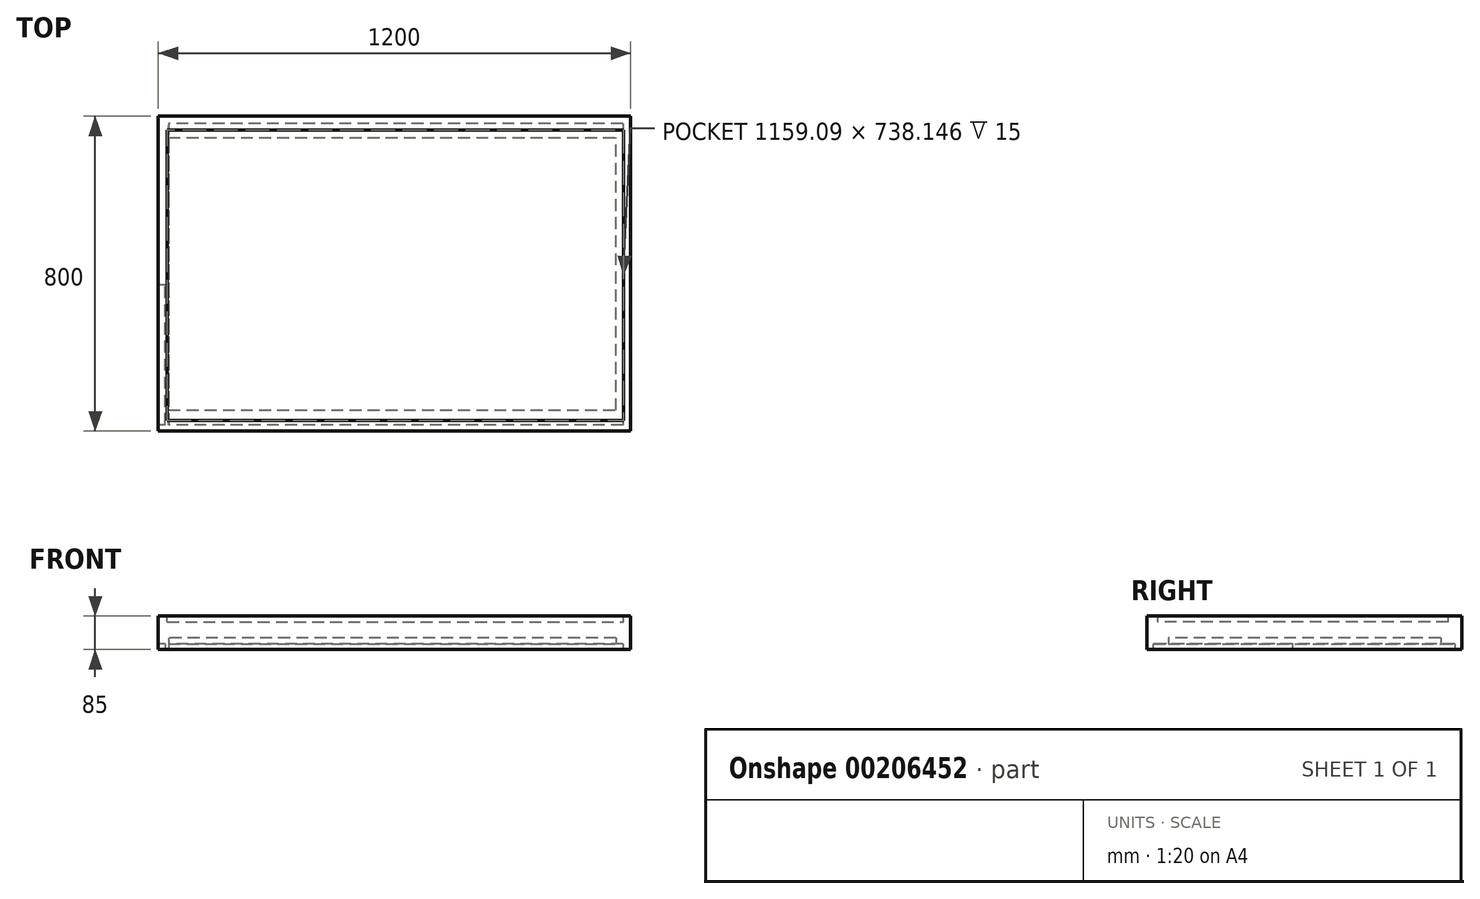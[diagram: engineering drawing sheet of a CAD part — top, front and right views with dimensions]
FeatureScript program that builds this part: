
annotation { "Feature Type Name" : "Feature", "Feature Type Description" : "" }
export const myFeature = defineFeature(function(context is Context, id is Id, definition is map)
    precondition{}
    {
        {
            var Q0;
            Q0=qCreatedBy(makeId("Top.planeOp"),FACE);
            var sketch = newSketch(context, id + "F0", { "sketchPlane" : qUnion([Q0])});
            skLineSegment(sketch, "E0.bottom", {"start": v(0, 0) * mm, "end": v(1200, 0) * mm});
            skLineSegment(sketch, "E0.top", {"start": v(0, 800) * mm, "end": v(1200, 800) * mm});
            skLineSegment(sketch, "E0.left", {"start": v(0, 0) * mm, "end": v(0, 800) * mm});
            skLineSegment(sketch, "E0.right", {"start": v(1200, 0) * mm, "end": v(1200, 800) * mm});
            skSolve(sketch);
        }
        {
            var Q0;
            Q0=makeQuery(id+"F0.imprint","IMPRINT",FACE,{"disambiguationData":[TD([[makeQuery(id+"F0.imprint","IMPRINT",EDGE,{"derivedFrom":sQuery(id+"F0.wireOp",EDGE,"E0.bottom")}),1.0]])]});
            extrude(context, id + "F1", {"entities" : qUnion([Q0]), "depth" : 60 * mm});
        }
        {
            var Q0;
            Q0=makeQuery(id+"F1.opExtrude","CAP_FACE",FACE,{"disambiguationData":[OSD([sQuery(id+"F0.wireOp",EDGE,"E0.bottom"),sQuery(id+"F0.wireOp",EDGE,"E0.top"),sQuery(id+"F0.wireOp",EDGE,"E0.left"),sQuery(id+"F0.wireOp",EDGE,"E0.right")])],"isStart":false});
            var sketch = newSketch(context, id + "F2", { "sketchPlane" : qUnion([Q0])});
            skLineSegment(sketch, "E1.bottom", {"start": v(37.83, 41.32) * mm, "end": v(1170.7, 41.32) * mm});
            skLineSegment(sketch, "E1.top", {"start": v(37.83, 752.02) * mm, "end": v(1170.7, 752.02) * mm});
            skLineSegment(sketch, "E1.left", {"start": v(37.83, 41.32) * mm, "end": v(37.83, 752.02) * mm});
            skLineSegment(sketch, "E1.right", {"start": v(1170.7, 41.32) * mm, "end": v(1170.7, 752.02) * mm});
            skSolve(sketch);
        }
        {
            var Q0;
            Q0=sQuery(id+"F2.wireOp",EDGE,"E1.top");
            var Q1;
            Q1=sQuery(id+"F2.wireOp",EDGE,"E1.left");
            var Q2;
            Q2=sQuery(id+"F2.wireOp",EDGE,"E1.bottom");
            var Q3;
            Q3=sQuery(id+"F2.wireOp",EDGE,"E1.right");
            extrude(context, id + "F3", {"bodyType" : ToolBodyType.SURFACE, "surfaceEntities" : qUnion([Q0, Q1, Q2, Q3]), "depth" : 30 * mm});
        }
        {
            var Q0;
            Q0=makeQuery(id+"F1.opExtrude","CAP_FACE",FACE,{"disambiguationData":[OSD([sQuery(id+"F0.wireOp",EDGE,"E0.bottom"),sQuery(id+"F0.wireOp",EDGE,"E0.top"),sQuery(id+"F0.wireOp",EDGE,"E0.left"),sQuery(id+"F0.wireOp",EDGE,"E0.right")])],"isStart":true});
            extrude(context, id + "F4", {"entities" : qUnion([Q0]), "operationType" : NewBodyOperationType.ADD, "depth" : 25 * mm});
        }
        {
            var Q0;
            Q0=makeQuery(id+"F4.opExtrude","CAP_FACE",FACE,{"disambiguationData":[OSD([sQuery(id+"F0.wireOp",EDGE,"E0.bottom"),sQuery(id+"F0.wireOp",EDGE,"E0.top"),sQuery(id+"F0.wireOp",EDGE,"E0.left"),sQuery(id+"F0.wireOp",EDGE,"E0.right")])],"isStart":false});
            var sketch = newSketch(context, id + "F5", { "sketchPlane" : qUnion([Q0])});
            skLineSegment(sketch, "E2.bottom", {"start": v(1162.82, -746.26) * mm, "end": v(25.87, -746.26) * mm});
            skLineSegment(sketch, "E2.top", {"start": v(1162.82, -53.64) * mm, "end": v(25.87, -53.64) * mm});
            skLineSegment(sketch, "E2.left", {"start": v(1162.82, -746.26) * mm, "end": v(1162.82, -53.64) * mm});
            skLineSegment(sketch, "E2.right", {"start": v(25.87, -746.26) * mm, "end": v(25.87, -53.64) * mm});
            skSolve(sketch);
        }
        {
            var Q0;
            Q0=makeQuery(id+"F5.imprint","IMPRINT",FACE,{"disambiguationData":[TD([[makeQuery(id+"F5.imprint","IMPRINT",EDGE,{"derivedFrom":sQuery(id+"F5.wireOp",EDGE,"E2.bottom")}),-1.0]])]});
            extrude(context, id + "F6", {"entities" : qUnion([Q0]), "operationType" : NewBodyOperationType.REMOVE, "oppositeDirection" : true, "depth" : 30 * mm});
        }
        {
            var Q0;
            Q0=makeQuery(id+"F1.opExtrude","CAP_FACE",FACE,{"disambiguationData":[OSD([sQuery(id+"F0.wireOp",EDGE,"E0.bottom"),sQuery(id+"F0.wireOp",EDGE,"E0.top"),sQuery(id+"F0.wireOp",EDGE,"E0.left"),sQuery(id+"F0.wireOp",EDGE,"E0.right")])],"isStart":false});
            var sketch = newSketch(context, id + "F7", { "sketchPlane" : qUnion([Q0])});
            skLineSegment(sketch, "E3.bottom", {"start": v(22.8, 765.04) * mm, "end": v(1181.9, 765.04) * mm});
            skLineSegment(sketch, "E3.top", {"start": v(22.8, 26.9) * mm, "end": v(1181.9, 26.9) * mm});
            skLineSegment(sketch, "E3.left", {"start": v(22.8, 765.04) * mm, "end": v(22.8, 26.9) * mm});
            skLineSegment(sketch, "E3.right", {"start": v(1181.9, 765.04) * mm, "end": v(1181.9, 26.9) * mm});
            skSolve(sketch);
        }
        {
            var Q0;
            Q0=makeQuery(id+"F7.imprint","IMPRINT",FACE,{"disambiguationData":[TD([[makeQuery(id+"F7.imprint","IMPRINT",EDGE,{"derivedFrom":sQuery(id+"F7.wireOp",EDGE,"E3.bottom")}),-1.0]])]});
            extrude(context, id + "F8", {"entities" : qUnion([Q0]), "operationType" : NewBodyOperationType.REMOVE, "oppositeDirection" : true, "depth" : 15 * mm});
        }
        {
            var Q0;
            Q0=makeQuery(id+"F4.opExtrude","CAP_FACE",FACE,{"disambiguationData":[OSD([sQuery(id+"F0.wireOp",EDGE,"E0.bottom"),sQuery(id+"F0.wireOp",EDGE,"E0.top"),sQuery(id+"F0.wireOp",EDGE,"E0.left"),sQuery(id+"F0.wireOp",EDGE,"E0.right")])],"isStart":false});
            var sketch = newSketch(context, id + "F9", { "sketchPlane" : qUnion([Q0])});
            skLineSegment(sketch, "E4.bottom", {"start": v(25.87, -31.78) * mm, "end": v(1008.33, -31.78) * mm});
            skLineSegment(sketch, "E4.top", {"start": v(25.87, -622.3) * mm, "end": v(1008.33, -622.3) * mm});
            skLineSegment(sketch, "E4.left", {"start": v(25.87, -31.78) * mm, "end": v(25.87, -622.3) * mm});
            skLineSegment(sketch, "E4.right", {"start": v(1008.33, -31.78) * mm, "end": v(1008.33, -622.3) * mm});
            skLineSegment(sketch, "E5.bottom", {"start": v(1179.9, -781.9) * mm, "end": v(25.87, -781.9) * mm});
            skLineSegment(sketch, "E5.top", {"start": v(1179.9, -15.82) * mm, "end": v(25.87, -15.82) * mm});
            skLineSegment(sketch, "E5.left", {"start": v(1179.9, -781.9) * mm, "end": v(1179.9, -15.82) * mm});
            skLineSegment(sketch, "E5.right", {"start": v(25.87, -781.9) * mm, "end": v(25.87, -15.82) * mm});
            skLineSegment(sketch, "E6.bottom", {"start": v(16.82, -15.82) * mm, "end": v(-180.68, -15.82) * mm});
            skLineSegment(sketch, "E6.top", {"start": v(16.82, -370.93) * mm, "end": v(-180.68, -370.93) * mm});
            skLineSegment(sketch, "E6.left", {"start": v(16.82, -15.82) * mm, "end": v(16.82, -370.93) * mm});
            skLineSegment(sketch, "E6.right", {"start": v(-180.68, -15.82) * mm, "end": v(-180.68, -370.93) * mm});
            skSolve(sketch);
        }
        {
            var Q0;
            {var subQ0=sQuery(id+"F9.wireOp",EDGE,"E6.right");Q0=makeQuery(id+"F9.imprint","IMPRINT",FACE,{"disambiguationData":[TD([[makeQuery(id+"F9.imprint","IMPRINT",EDGE,{"derivedFrom":subQ0}),1.0]])]});}
            var Q1;
            {var subQ0=sQuery(id+"F9.wireOp",EDGE,"E6.left");Q1=makeQuery(id+"F9.imprint","IMPRINT",FACE,{"disambiguationData":[TD([[makeQuery(id+"F9.imprint","IMPRINT",EDGE,{"derivedFrom":subQ0}),-1.0]])]});}
            var Q2;
            {var subQ0=sQuery(id+"F9.wireOp",EDGE,"E4.bottom");Q2=makeQuery(id+"F9.imprint","IMPRINT",FACE,{"disambiguationData":[TD([[makeQuery(id+"F9.imprint","IMPRINT",EDGE,{"derivedFrom":subQ0}),-1.0]])]});}
            var Q3;
            {var subQ2=sQuery(id+"F9.wireOp",EDGE,"E4.top");Q3=makeQuery(id+"F9.imprint","IMPRINT",FACE,{"disambiguationData":[TD([[makeQuery(id+"F9.imprint","IMPRINT",EDGE,{"derivedFrom":subQ2}),-1.0]])]});}
            var Q4;
            {var subQ0=sQuery(id+"F9.wireOp",EDGE,"E4.top");Q4=makeQuery(id+"F9.imprint","IMPRINT",FACE,{"disambiguationData":[TD([[makeQuery(id+"F9.imprint","IMPRINT",EDGE,{"derivedFrom":subQ0}),1.0]])]});}
            var Q5;
            {var subQ5=sQuery(id+"F9.wireOp",EDGE,"E4.bottom");Q5=makeQuery(id+"F9.imprint","IMPRINT",FACE,{"disambiguationData":[TD([[makeQuery(id+"F9.imprint","IMPRINT",EDGE,{"derivedFrom":subQ5}),1.0]])]});}
            extrude(context, id + "F10", {"entities" : qUnion([Q0, Q1, Q2, Q3, Q4, Q5]), "operationType" : NewBodyOperationType.REMOVE, "oppositeDirection" : true, "depth" : 15 * mm});
        }
    });
